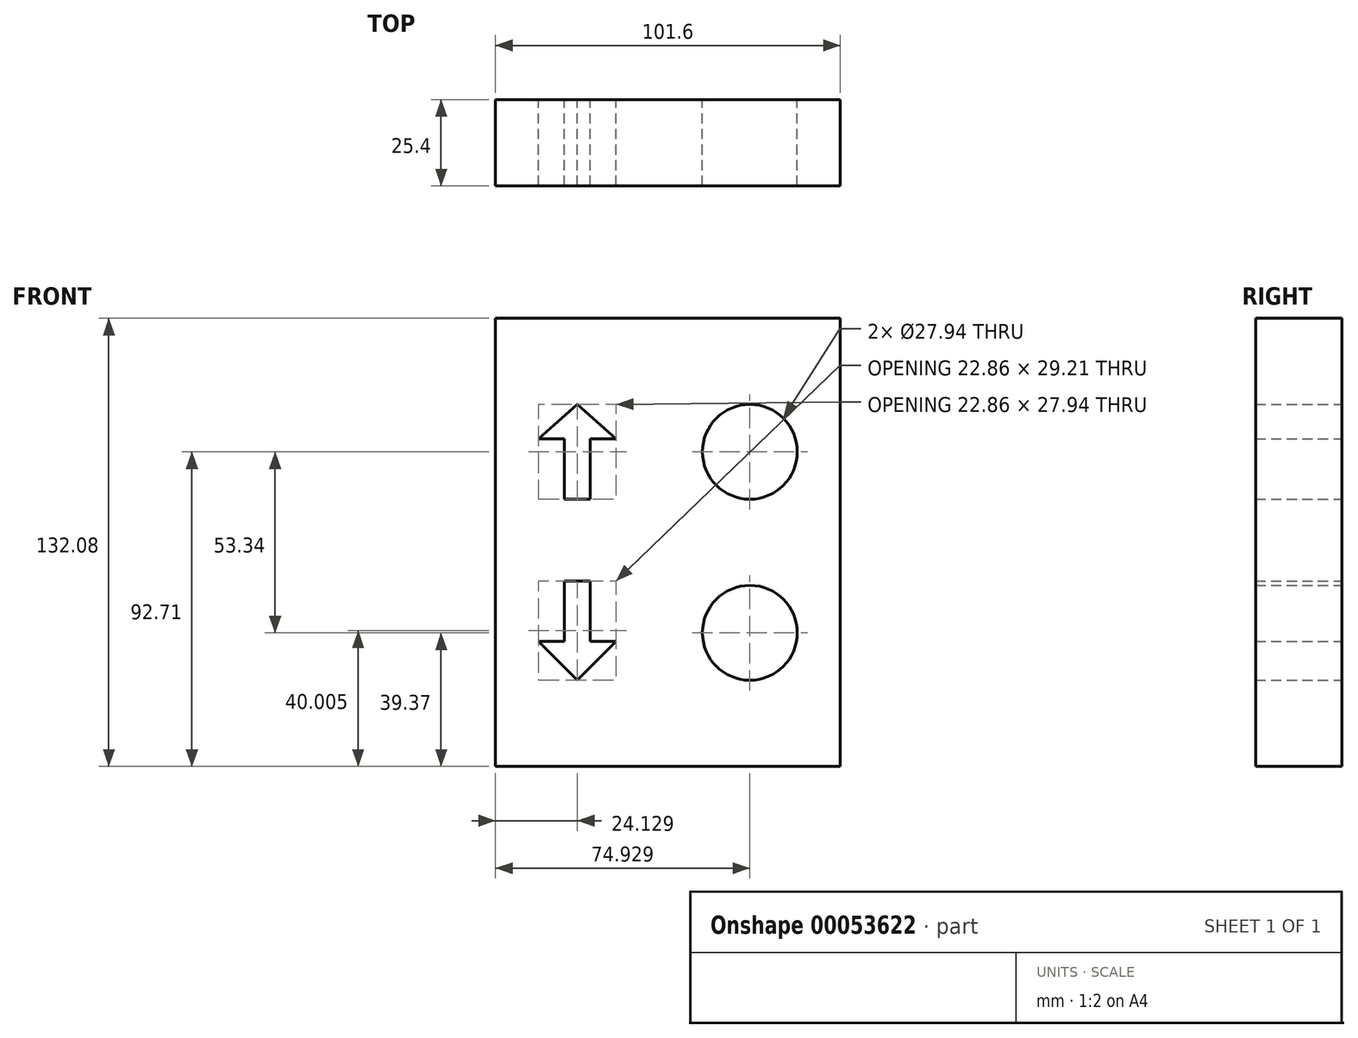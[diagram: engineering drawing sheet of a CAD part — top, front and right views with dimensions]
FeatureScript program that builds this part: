
annotation { "Feature Type Name" : "Feature", "Feature Type Description" : "" }
export const myFeature = defineFeature(function(context is Context, id is Id, definition is map)
    precondition{}
    {
        {
            var Q0;
            Q0=qCreatedBy(makeId("Front.planeOp"),FACE);
            var sketch = newSketch(context, id + "F0", { "sketchPlane" : qUnion([Q0])});
            skLineSegment(sketch, "E0.bottom", {"start": v(-66.08, 77.47) * mm, "end": v(35.52, 77.47) * mm});
            skLineSegment(sketch, "E0.top", {"start": v(-66.08, -54.6) * mm, "end": v(35.52, -54.6) * mm});
            skLineSegment(sketch, "E0.left", {"start": v(-66.08, 77.47) * mm, "end": v(-66.08, -54.6) * mm});
            skLineSegment(sketch, "E0.right", {"start": v(35.52, 77.47) * mm, "end": v(35.52, -54.6) * mm});
            skCircle(sketch, "E1", {"center": v(8.85, 38.1) * mm, "radius": 13.97 * mm});
            skCircle(sketch, "E2", {"center": v(8.85, -15.24) * mm, "radius": 13.97 * mm});
            skLineSegment(sketch, "E3", {"start": v(-41.95, 52.07) * mm, "end": v(-53.38, 41.91) * mm});
            skLineSegment(sketch, "E4", {"start": v(-53.38, 41.91) * mm, "end": v(-45.76, 41.91) * mm});
            skLineSegment(sketch, "E5", {"start": v(-45.76, 41.91) * mm, "end": v(-45.76, 24.13) * mm});
            skLineSegment(sketch, "E6", {"start": v(-45.76, 24.13) * mm, "end": v(-38.14, 24.13) * mm});
            skLineSegment(sketch, "E7", {"start": v(-38.14, 24.13) * mm, "end": v(-38.14, 41.91) * mm});
            skLineSegment(sketch, "E8", {"start": v(-38.14, 41.91) * mm, "end": v(-30.52, 41.91) * mm});
            skLineSegment(sketch, "E9", {"start": v(-30.52, 41.91) * mm, "end": v(-41.95, 52.07) * mm});
            skLineSegment(sketch, "E10", {"start": v(-53.38, -17.78) * mm, "end": v(-41.95, -29.2) * mm});
            skLineSegment(sketch, "E11", {"start": v(-41.95, -29.21) * mm, "end": v(-30.52, -17.78) * mm});
            skLineSegment(sketch, "E12", {"start": v(-30.52, -17.78) * mm, "end": v(-38.14, -17.78) * mm});
            skLineSegment(sketch, "E13", {"start": v(-38.14, -17.78) * mm, "end": v(-38.14, 0) * mm});
            skLineSegment(sketch, "E14", {"start": v(-38.14, 0) * mm, "end": v(-45.76, 0) * mm});
            skLineSegment(sketch, "E15", {"start": v(-45.76, 0) * mm, "end": v(-45.76, -17.78) * mm});
            skLineSegment(sketch, "E16", {"start": v(-45.76, -17.78) * mm, "end": v(-53.38, -17.78) * mm});
            skPoint(sketch, "E17.visualSharp", {"position": v(35.52, 77.47) * mm});
            skLineSegment(sketch, "E17.filletArc", {"start": v(35.52, 77.47) * mm, "end": v(35.52, 77.47) * mm});
            skPoint(sketch, "E18.visualSharp", {"position": v(35.52, -54.6) * mm});
            skLineSegment(sketch, "E18.filletArc", {"start": v(35.52, -54.6) * mm, "end": v(35.52, -54.6) * mm});
            skPoint(sketch, "E19.visualSharp", {"position": v(-66.08, -54.6) * mm});
            skLineSegment(sketch, "E19.filletArc", {"start": v(-66.08, -54.6) * mm, "end": v(-66.08, -54.6) * mm});
            skPoint(sketch, "E20.visualSharp", {"position": v(-66.08, 77.47) * mm});
            skLineSegment(sketch, "E20.filletArc", {"start": v(-66.08, 77.47) * mm, "end": v(-66.08, 77.47) * mm});
            skSolve(sketch);
        }
        {
            var Q0;
            Q0=makeQuery(id+"F0.imprint","IMPRINT",FACE,{"disambiguationData":[TD([[makeQuery(id+"F0.imprint","IMPRINT",EDGE,{"derivedFrom":sQuery(id+"F0.wireOp",EDGE,"E0.bottom")}),-1.0]])]});
            extrude(context, id + "F1", {"entities" : qUnion([Q0]), "depth" : 25.4 * mm});
        }
    });
